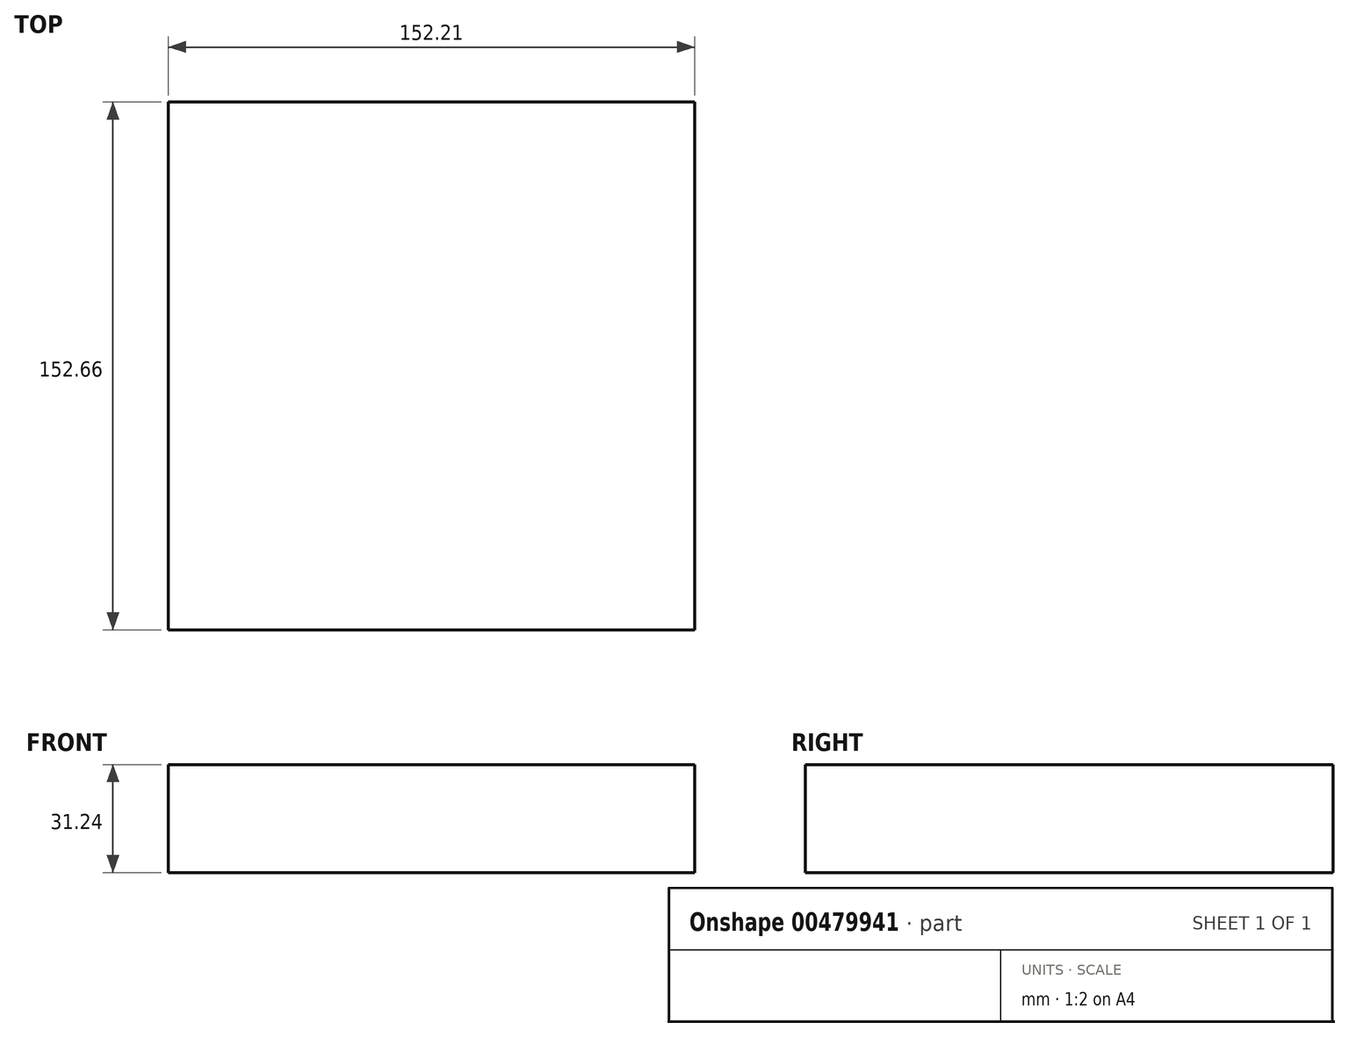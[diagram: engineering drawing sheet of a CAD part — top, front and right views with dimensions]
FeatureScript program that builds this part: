
annotation { "Feature Type Name" : "Feature", "Feature Type Description" : "" }
export const myFeature = defineFeature(function(context is Context, id is Id, definition is map)
    precondition{}
    {
        {
            var Q0;
            Q0=qCreatedBy(makeId("Top.planeOp"),FACE);
            var sketch = newSketch(context, id + "F0", { "sketchPlane" : qUnion([Q0])});
            skLineSegment(sketch, "E0.bottom", {"start": v(75.59, -76.44) * mm, "end": v(-76.62, -76.44) * mm});
            skLineSegment(sketch, "E0.top", {"start": v(75.59, 76.22) * mm, "end": v(-76.62, 76.22) * mm});
            skLineSegment(sketch, "E0.left", {"start": v(75.59, -76.44) * mm, "end": v(75.59, 76.22) * mm});
            skLineSegment(sketch, "E0.right", {"start": v(-76.62, -76.44) * mm, "end": v(-76.62, 76.22) * mm});
            skSolve(sketch);
        }
        {
            var Q0;
            Q0=makeQuery(id+"F0.imprint","IMPRINT",FACE,{"disambiguationData":[TD([[makeQuery(id+"F0.imprint","IMPRINT",EDGE,{"derivedFrom":sQuery(id+"F0.wireOp",EDGE,"E0.bottom")}),-1.0]])]});
            extrude(context, id + "F1", {"entities" : qUnion([Q0]), "oppositeDirection" : true, "depth" : 31.24 * mm});
        }
    });
